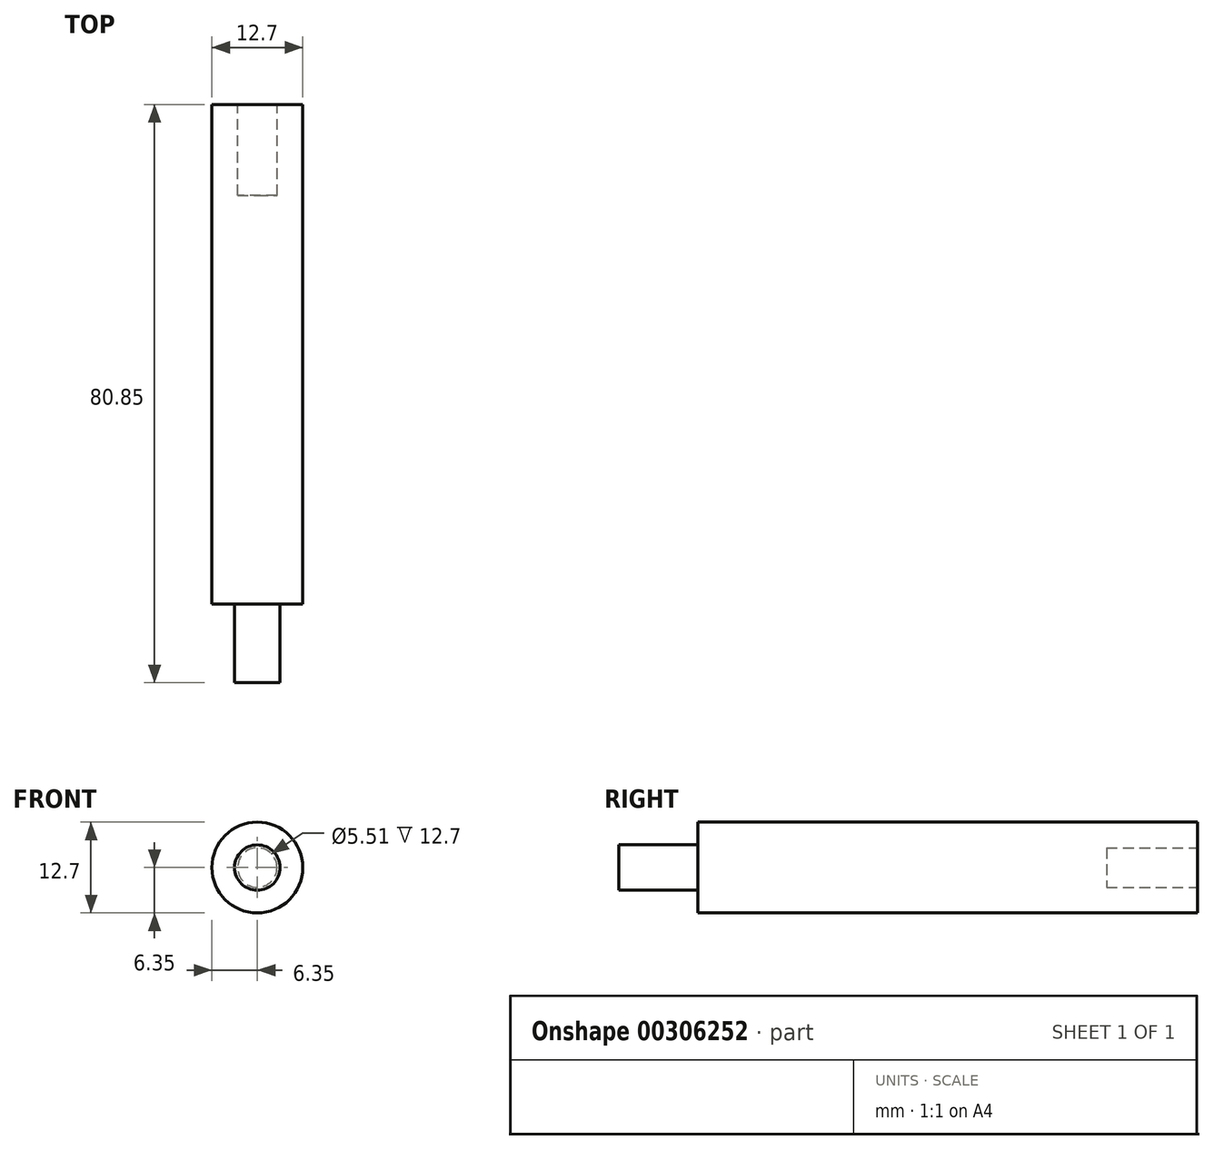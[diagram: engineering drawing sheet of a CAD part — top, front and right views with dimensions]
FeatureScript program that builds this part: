
annotation { "Feature Type Name" : "Feature", "Feature Type Description" : "" }
export const myFeature = defineFeature(function(context is Context, id is Id, definition is map)
    precondition{}
    {
        {
            var Q0;
            Q0=qCreatedBy(makeId("Front.planeOp"),FACE);
            var sketch = newSketch(context, id + "F0", { "sketchPlane" : qUnion([Q0])});
            skCircle(sketch, "E0", {"center": v(0, 0) * mm, "radius": 6.35 * mm});
            skSolve(sketch);
        }
        {
            var Q0;
            Q0 = qSketchRegion(id + "F0", true);
            extrude(context, id + "F1", {"entities" : qUnion([Q0]), "depth" : 69.85 * mm});
        }
        {
            var Q0;
            Q0=makeQuery(id+"F1.opExtrude","CAP_FACE",FACE,{"disambiguationData":[OSD([sQuery(id+"F0.wireOp",EDGE,"E0")])],"isStart":false});
            var sketch = newSketch(context, id + "F2", { "sketchPlane" : qUnion([Q0])});
            skCircle(sketch, "E1", {"center": v(0, 0) * mm, "radius": 3.18 * mm});
            skSolve(sketch);
        }
        {
            var Q0;
            Q0 = qSketchRegion(id + "F2", true);
            extrude(context, id + "F3", {"entities" : qUnion([Q0]), "operationType" : NewBodyOperationType.ADD, "depth" : 11 * mm});
        }
        {
            var Q0;
            Q0=makeQuery(id+"F1.opExtrude","CAP_FACE",FACE,{"disambiguationData":[OSD([sQuery(id+"F0.wireOp",EDGE,"E0")])],"isStart":true});
            var sketch = newSketch(context, id + "F4", { "sketchPlane" : qUnion([Q0])});
            skCircle(sketch, "E2", {"center": v(0, 0) * mm, "radius": 2.76 * mm});
            skSolve(sketch);
        }
        {
            var Q0;
            Q0=makeQuery(id+"F4.imprint","IMPRINT",FACE,{"disambiguationData":[TD([[makeQuery(id+"F4.imprint","IMPRINT",EDGE,{"derivedFrom":sQuery(id+"F4.wireOp",EDGE,"E2")}),1.0]])]});
            extrude(context, id + "F5", {"entities" : qUnion([Q0]), "operationType" : NewBodyOperationType.REMOVE, "oppositeDirection" : true, "depth" : 12.7 * mm});
        }
    });
